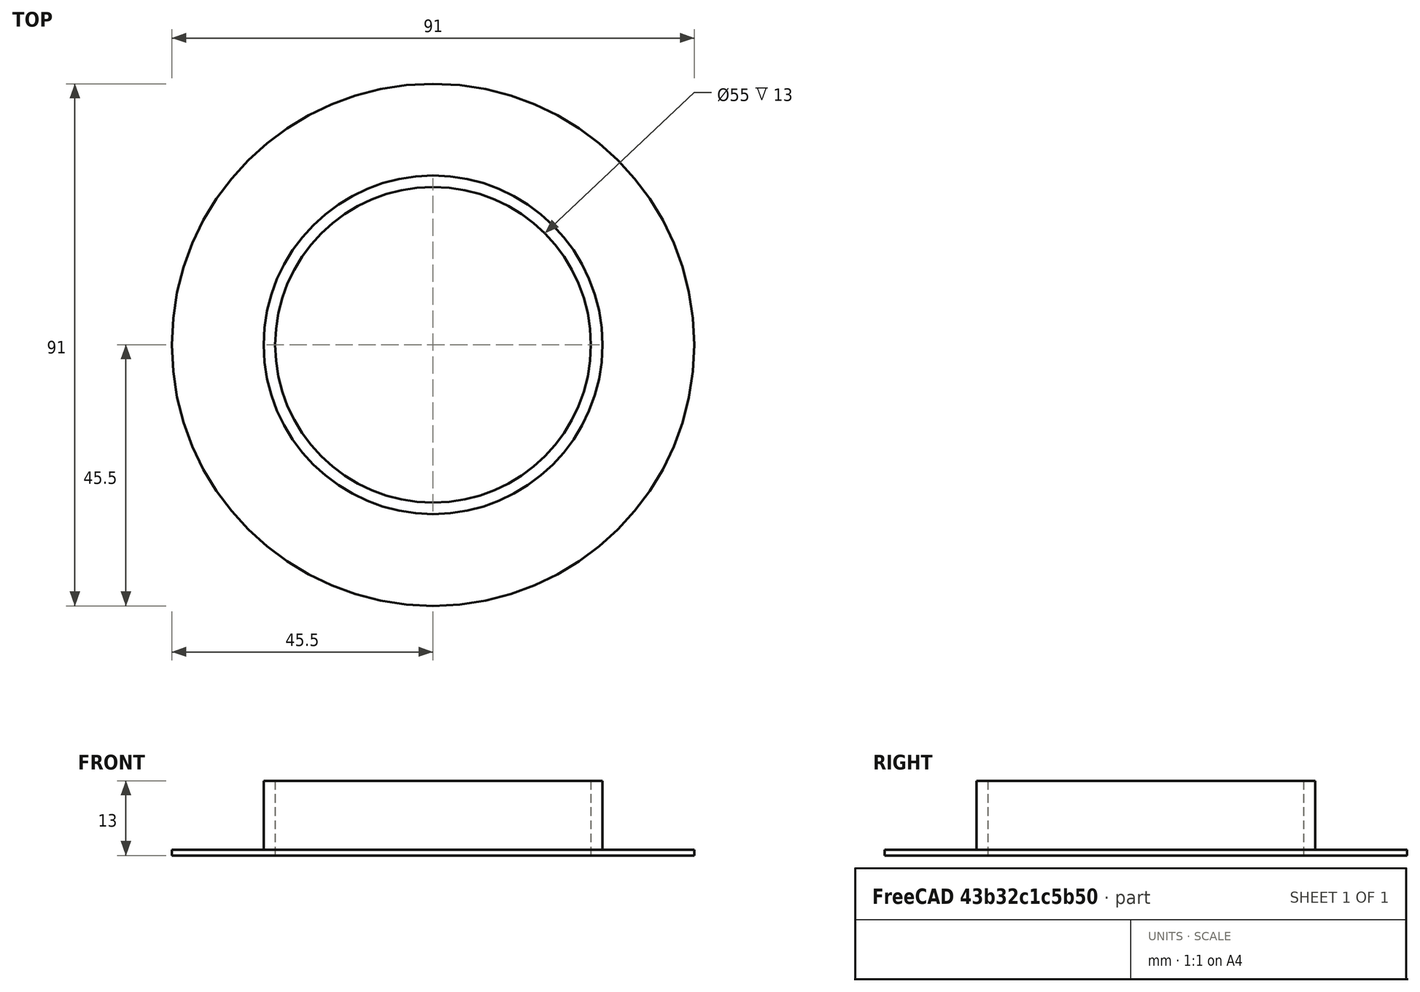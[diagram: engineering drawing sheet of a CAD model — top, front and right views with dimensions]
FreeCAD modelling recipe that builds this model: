
FCSTD DOCUMENT  (FreeCAD 0.16R6712 (Git))
Label: ASPIRA_01
License: All rights reserved
LicenseURL: http://en.wikipedia.org/wiki/All_rights_reserved
objects: Part::Part2DObjectPython×1, Sketcher::SketchObject×1, Part::Revolution×1
note: 3 computed .brp shape members not serialized (recipe doc carries the construction recipe); baked Part::Feature solids carry a one-line shape summary decoded from their .brp

FEATURE [Part::Part2DObjectPython] Line  # Draft 2D object (typed FeaturePython)
  ChamferSize = 0
  Closed = false
  End = (0,0,10)
  FilletRadius = 0
  Length = 10
  MakeFace = true
  Points = (2) [(0,0,0),(0,0,10)]
  Start = (0,0,0)
  Subdivisions = 0
FEATURE [Sketcher::SketchObject] Sketch
  Placement = pos=(0,0,0) rot=(-1,0,0;4.71239rad)
  sketch-geometry (7):
    g0: LineSegment [constr] StartX=0 StartY=0 StartZ=0 EndX=27.5 EndY=0 EndZ=0
    g1: LineSegment StartX=27.5 StartY=0 StartZ=0 EndX=45.5 EndY=0 EndZ=0
    g2: LineSegment StartX=45.5 StartY=0 StartZ=0 EndX=45.5 EndY=1 EndZ=0
    g3: LineSegment StartX=29.5 StartY=13 StartZ=0 EndX=27.5 EndY=13 EndZ=0
    g4: LineSegment StartX=27.5 StartY=13 StartZ=0 EndX=27.5 EndY=0 EndZ=0
    g5: LineSegment StartX=45.5 StartY=1 StartZ=0 EndX=29.5 EndY=1 EndZ=0
    g6: LineSegment StartX=29.5 StartY=1 StartZ=0 EndX=29.5 EndY=13 EndZ=0
  constraints (20):
    c: Coincident(g0,g-1)
    c: PointOnObject(g0,g-1)
    c: Distance(g0) = 27.5
    c: Coincident(g1,g2)
    c: Coincident(g3,g4)
    c: Coincident(g4,g1)
    c: Horizontal(g1)
    c: Horizontal(g3)
    c: Vertical(g2)
    c: Vertical(g4)
    c: Coincident(g1,g0)
    c: Coincident(g5,g6)
    c: Horizontal(g5)
    c: Vertical(g6)
    c: Coincident(g6,g3)
    c: Coincident(g5,g2)
    c: Distance(g4) = 13
    c: Distance(g1) = 18
    c: Distance(g2) = 1
    c: Distance(g3) = 2
FEATURE [Part::Revolution] Revolve
  Angle = 360
  Axis = (0,0,1)
  Base = (0,0,0)
  Solid = true
  Source = -> Sketch
